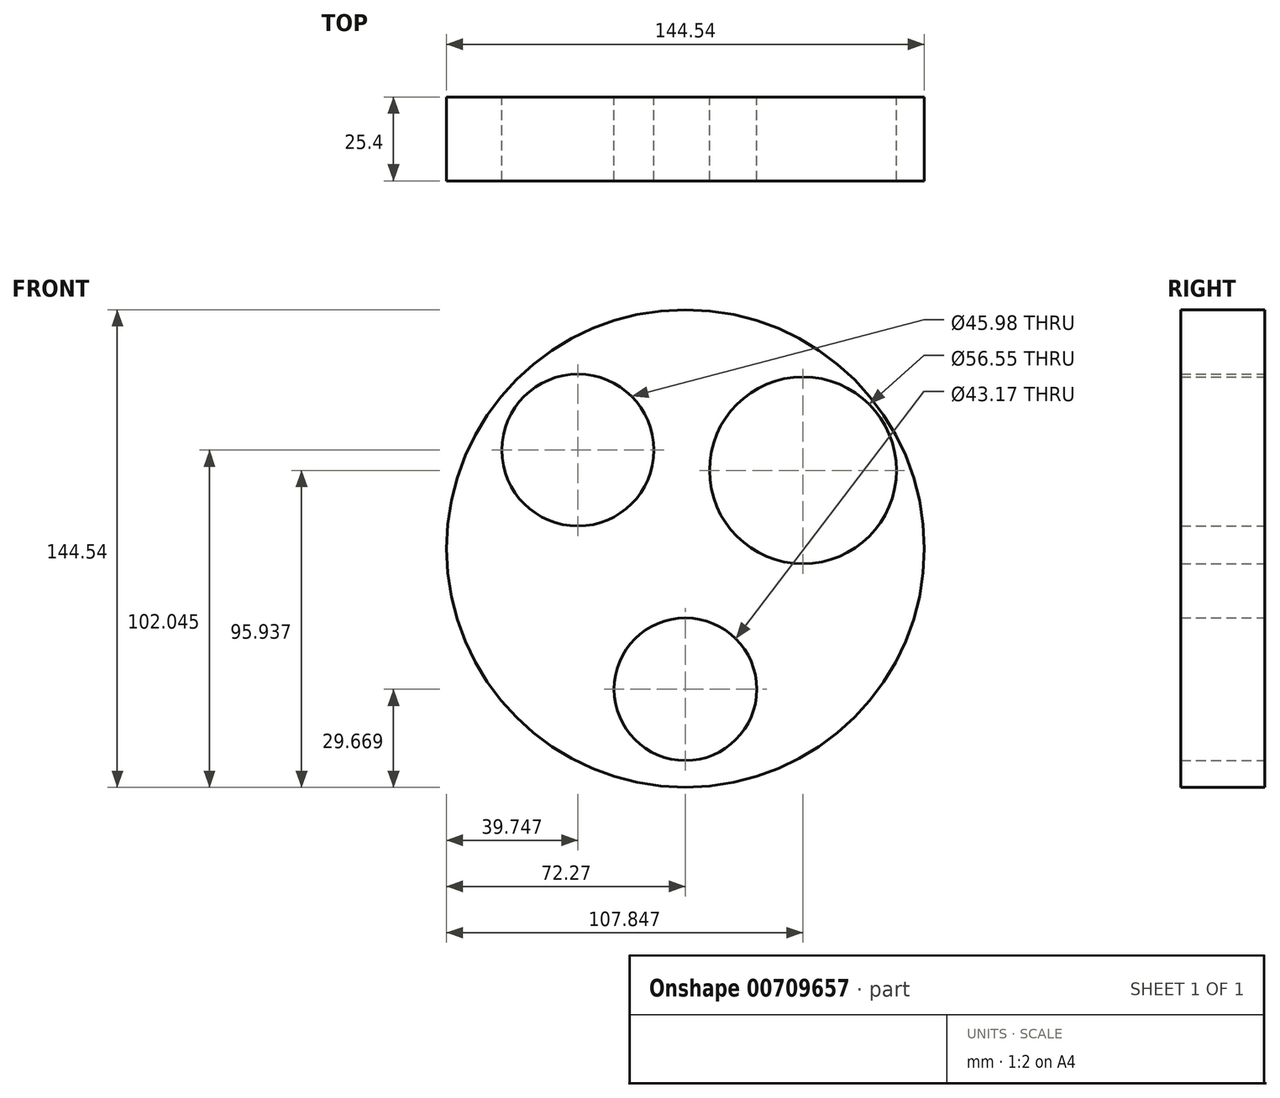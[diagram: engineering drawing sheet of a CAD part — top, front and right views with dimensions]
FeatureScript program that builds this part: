
annotation { "Feature Type Name" : "Feature", "Feature Type Description" : "" }
export const myFeature = defineFeature(function(context is Context, id is Id, definition is map)
    precondition{}
    {
        {
            var Q0;
            Q0=qCreatedBy(makeId("Front.planeOp"),FACE);
            var sketch = newSketch(context, id + "F0", { "sketchPlane" : qUnion([Q0])});
            skCircle(sketch, "E0", {"center": v(0, 0) * mm, "radius": 72.27 * mm});
            skCircle(sketch, "E1", {"center": v(-32.52, 29.77) * mm, "radius": 23 * mm});
            skCircle(sketch, "E2", {"center": v(35.58, 23.67) * mm, "radius": 28.28 * mm});
            skCircle(sketch, "E3", {"center": v(0, -42.6) * mm, "radius": 21.58 * mm});
            skSolve(sketch);
        }
        {
            var Q0;
            Q0=makeQuery(id+"F0.imprint","IMPRINT",FACE,{"disambiguationData":[TD([[makeQuery(id+"F0.imprint","IMPRINT",EDGE,{"derivedFrom":sQuery(id+"F0.wireOp",EDGE,"E0")}),1.0]])]});
            extrude(context, id + "F1", {"entities" : qUnion([Q0]), "depth" : 25.4 * mm, "offsetDistance" : 25.4 * mm});
        }
    });
